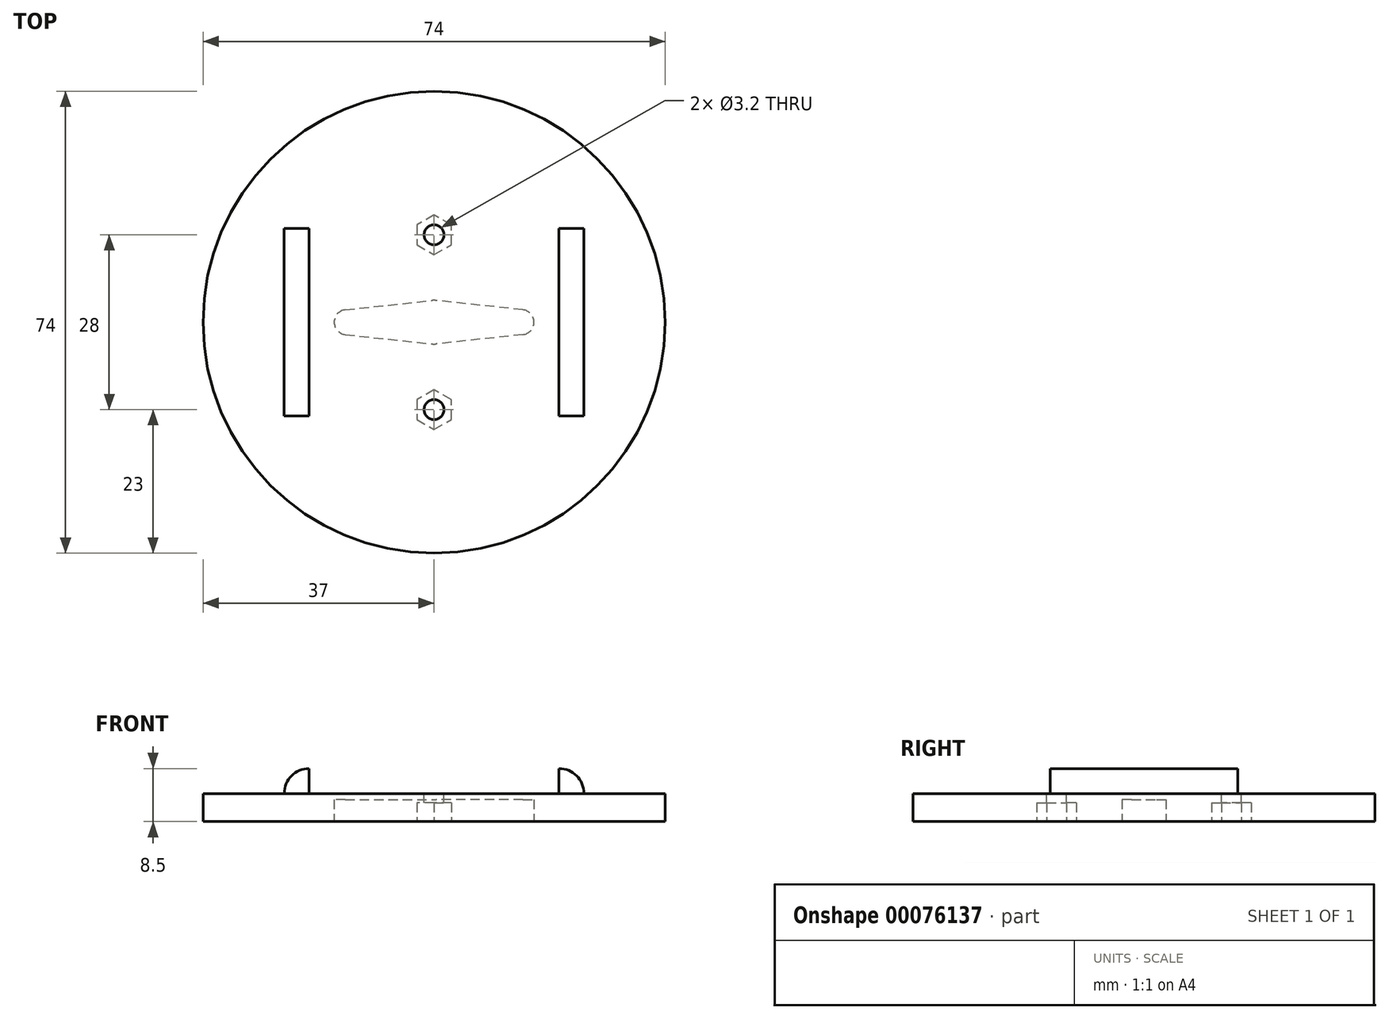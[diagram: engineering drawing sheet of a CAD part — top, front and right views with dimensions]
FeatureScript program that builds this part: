
annotation { "Feature Type Name" : "Feature", "Feature Type Description" : "" }
export const myFeature = defineFeature(function(context is Context, id is Id, definition is map)
    precondition{}
    {
        {
            var Q0;
            Q0=qCreatedBy(makeId("Top.planeOp"),FACE);
            var sketch = newSketch(context, id + "F0", { "sketchPlane" : qUnion([Q0])});
            skCircle(sketch, "E0", {"center": v(0, 0) * mm, "radius": 37 * mm});
            skSolve(sketch);
        }
        {
            var Q0;
            Q0=makeQuery(id+"F0.imprint","IMPRINT",FACE,{"disambiguationData":[TD([[makeQuery(id+"F0.imprint","IMPRINT",EDGE,{"derivedFrom":sQuery(id+"F0.wireOp",EDGE,"E0")}),1.0]])]});
            extrude(context, id + "F1", {"entities" : qUnion([Q0]), "depth" : 4.5 * mm});
        }
        {
            var Q0;
            Q0=makeQuery(id+"F1.opExtrude","CAP_FACE",FACE,{"disambiguationData":[OSD([sQuery(id+"F0.wireOp",EDGE,"E0")])],"isStart":true});
            var sketch = newSketch(context, id + "F2", { "sketchPlane" : qUnion([Q0])});
            skCircle(sketch, "E1", {"center": v(0, 0) * mm, "radius": 3.5 * mm});
            skLineSegment(sketch, "E2", {"start": v(0, 0) * mm, "end": v(0, 14) * mm});
            skCircle(sketch, "E3", {"center": v(0, 14) * mm, "radius": 2 * mm});
            skCircle(sketch, "E4.MirrorC", {"center": v(0, -14) * mm, "radius": 2 * mm});
            skLineSegment(sketch, "E5", {"start": v(-1.99, 14.21) * mm, "end": v(-3.48, 0.38) * mm});
            skLineSegment(sketch, "E6", {"start": v(1.99, 14.21) * mm, "end": v(3.48, 0.37) * mm});
            skLineSegment(sketch, "E7.MirrorCS", {"start": v(-1.99, -14.21) * mm, "end": v(-3.48, -0.38) * mm});
            skLineSegment(sketch, "E8.MirrorCS", {"start": v(1.99, -14.21) * mm, "end": v(3.48, -0.37) * mm});
            skSolve(sketch);
        }
        {
            var Q0;
            Q0 = qSketchRegion(id + "F2", true);
            extrude(context, id + "F3", {"entities" : qUnion([Q0]), "operationType" : NewBodyOperationType.REMOVE, "oppositeDirection" : true, "depth" : 3.5 * mm});
        }
        {
            var Q0;
            Q0=qCreatedBy(makeId("Right.planeOp"),FACE);
            var sketch = newSketch(context, id + "F4", { "sketchPlane" : qUnion([Q0])});
            skLineSegment(sketch, "E9.0", {"start": v(-37, 4.5) * mm, "end": v(37, 4.5) * mm});
            skLineSegment(sketch, "E10", {"start": v(20, 4.5) * mm, "end": v(20, 8.5) * mm});
            skArc(sketch, "E11", {"start": v(20, 8.5) * mm, "mid": v(22.83, 7.33) * mm, "end": v(24, 4.5) * mm});
            skLineSegment(sketch, "E12.MirrorCS", {"start": v(-20, 4.5) * mm, "end": v(-20, 8.5) * mm});
            skArc(sketch, "E13.MirrorCS", {"start": v(-20, 8.5) * mm, "mid": v(-22.83, 7.33) * mm, "end": v(-24, 4.5) * mm});
            skSolve(sketch);
        }
        {
            var Q0;
            {var subQ0=sQuery(id+"F4.wireOp",EDGE,"E12.MirrorCS");Q0=makeQuery(id+"F4.imprint","IMPRINT",FACE,{"disambiguationData":[TD([[makeQuery(id+"F4.imprint","IMPRINT",EDGE,{"derivedFrom":subQ0}),1.0]])]});}
            var Q1;
            {var subQ0=sQuery(id+"F4.wireOp",EDGE,"E10");Q1=makeQuery(id+"F4.imprint","IMPRINT",FACE,{"disambiguationData":[TD([[makeQuery(id+"F4.imprint","IMPRINT",EDGE,{"derivedFrom":subQ0}),-1.0]])]});}
            extrude(context, id + "F5", {"entities" : qUnion([Q0, Q1]), "operationType" : NewBodyOperationType.ADD, "depth" : 30 * mm, "symmetric" : true});
        }
        {
            var Q0;
            Q0=makeQuery(id+"F1.opExtrude","CAP_FACE",FACE,{"disambiguationData":[OSD([sQuery(id+"F0.wireOp",EDGE,"E0")])],"isStart":false});
            var sketch = newSketch(context, id + "F6", { "sketchPlane" : qUnion([Q0])});
            skCircle(sketch, "E14", {"center": v(-14, 0) * mm, "radius": 1.6 * mm});
            skCircle(sketch, "E15.MirrorC", {"center": v(14, 0) * mm, "radius": 1.6 * mm});
            skSolve(sketch);
        }
        {
            var Q0;
            Q0 = qSketchRegion(id + "F6", true);
            extrude(context, id + "F7", {"entities" : qUnion([Q0]), "operationType" : NewBodyOperationType.REMOVE, "endBound" : BoundingType.THROUGH_ALL, "oppositeDirection" : true, "depth" : 25 * mm});
        }
        {
            var Q0;
            Q0=makeQuery(id+"F1.opExtrude","CAP_FACE",FACE,{"disambiguationData":[OSD([sQuery(id+"F0.wireOp",EDGE,"E0")])],"isStart":true});
            var sketch = newSketch(context, id + "F8", { "sketchPlane" : qUnion([Q0])});
            skCircle(sketch, "E16.cCircle", {"center": v(14, 0) * mm, "radius": 2.75 * mm, "construction": true});
            skLineSegment(sketch, "E16.0", {"start": v(10.82, 0) * mm, "end": v(12.41, 2.75) * mm});
            skLineSegment(sketch, "E16.1", {"start": v(12.41, 2.75) * mm, "end": v(15.59, 2.75) * mm});
            skLineSegment(sketch, "E16.2", {"start": v(15.59, 2.75) * mm, "end": v(17.18, 0) * mm});
            skLineSegment(sketch, "E16.3", {"start": v(17.18, 0) * mm, "end": v(15.59, -2.75) * mm});
            skLineSegment(sketch, "E16.4", {"start": v(15.59, -2.75) * mm, "end": v(12.41, -2.75) * mm});
            skLineSegment(sketch, "E16.5", {"start": v(12.41, -2.75) * mm, "end": v(10.82, 0) * mm});
            skPoint(sketch, "E16.0.midPoint", {"position": v(11.62, 1.38) * mm});
            skLineSegment(sketch, "E17", {"start": v(10.82, 0) * mm, "end": v(17.18, 0) * mm, "construction": true});
            skCircle(sketch, "E18.cCircle", {"center": v(-14, 0) * mm, "radius": 2.75 * mm, "construction": true});
            skLineSegment(sketch, "E18.0", {"start": v(-10.82, 0) * mm, "end": v(-12.41, -2.75) * mm});
            skLineSegment(sketch, "E18.1", {"start": v(-12.41, -2.75) * mm, "end": v(-15.59, -2.75) * mm});
            skLineSegment(sketch, "E18.2", {"start": v(-15.59, -2.75) * mm, "end": v(-17.18, 0) * mm});
            skLineSegment(sketch, "E18.3", {"start": v(-17.18, 0) * mm, "end": v(-15.59, 2.75) * mm});
            skLineSegment(sketch, "E18.4", {"start": v(-15.59, 2.75) * mm, "end": v(-12.41, 2.75) * mm});
            skLineSegment(sketch, "E18.5", {"start": v(-12.41, 2.75) * mm, "end": v(-10.82, 0) * mm});
            skPoint(sketch, "E18.0.midPoint", {"position": v(-11.62, -1.38) * mm});
            skLineSegment(sketch, "E19", {"start": v(-10.82, 0) * mm, "end": v(-17.18, 0) * mm, "construction": true});
            skSolve(sketch);
        }
        {
            var Q0;
            Q0 = qSketchRegion(id + "F8", true);
            extrude(context, id + "F9", {"entities" : qUnion([Q0]), "operationType" : NewBodyOperationType.REMOVE, "oppositeDirection" : true, "depth" : 3 * mm});
        }
        {
            var Q0;
            Q0=qCreatedBy(makeId("Right.planeOp"),FACE);
            var sketch = newSketch(context, id + "F10", { "sketchPlane" : qUnion([Q0])});
            skLineSegment(sketch, "E20", {"start": v(0, -3.18) * mm, "end": v(0, 73.83) * mm, "construction": true});
            skSolve(sketch);
        }
        {
            var Q0;
            Q0=makeQuery(id+"F1.opExtrude","SWEPT_BODY",BODY,{"disambiguationData":[OSD([sQuery(id+"F0.wireOp",EDGE,"E0")])]});
            var Q1;
            Q1=sQuery(id+"F10.wireOp",EDGE,"E20");
            var Q2;
            Q2=sQuery(id+"F10.wireOp",EDGE,"E20");
            transform(context, id + "F11", {"entities" : qUnion([Q0]), "transformType" : TransformType.ROTATION, "transformAxis" : qUnion([Q2]), "angle" : 90 * degree, "makeCopy" : false});
        }
    });
